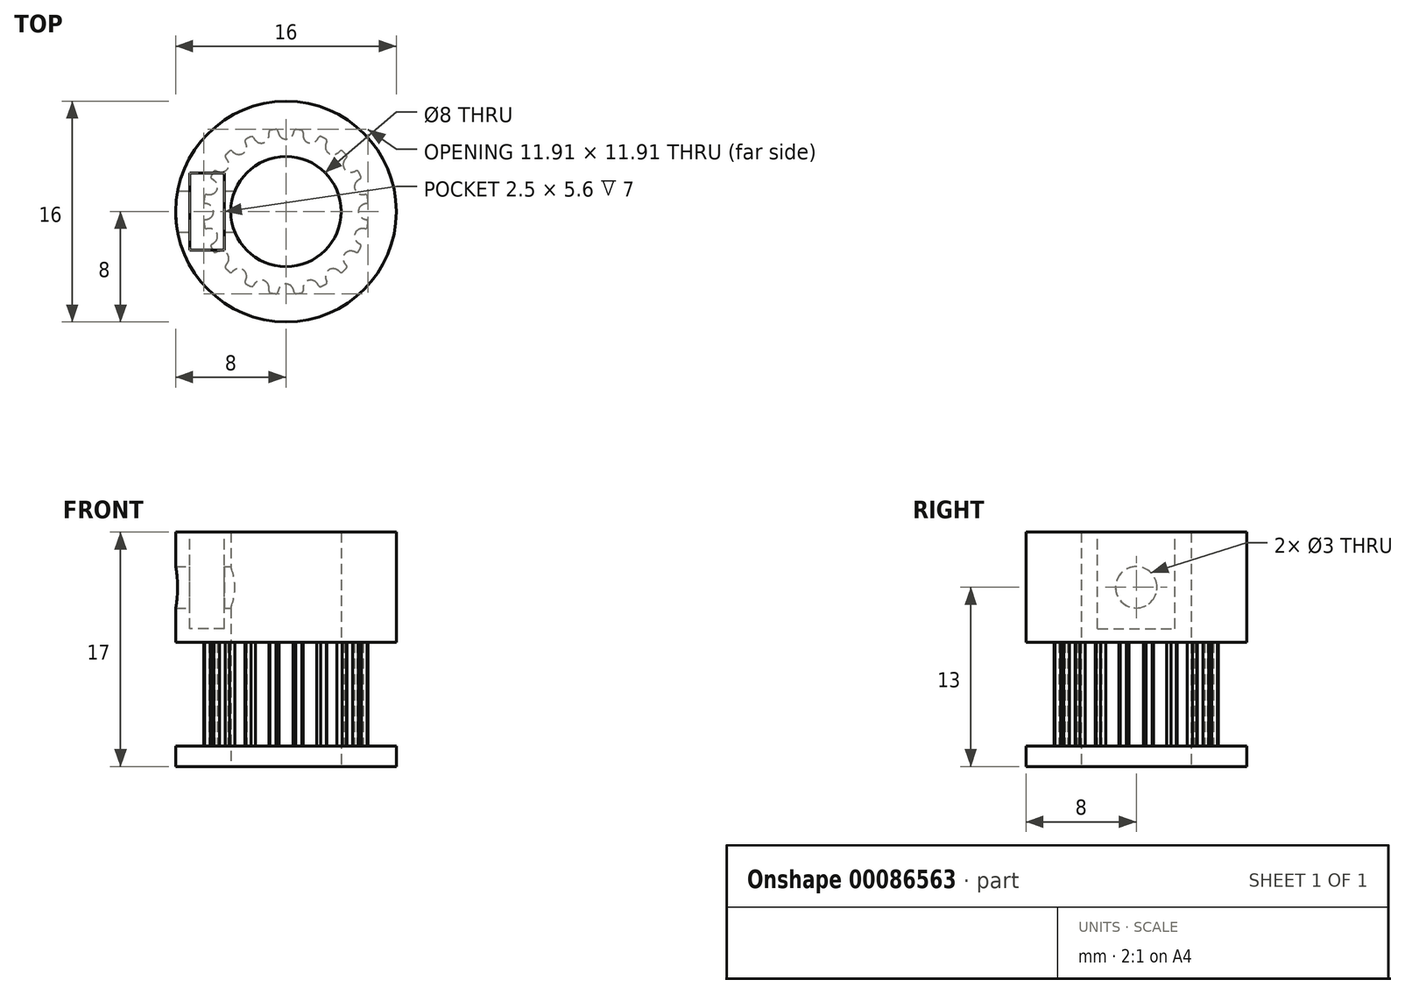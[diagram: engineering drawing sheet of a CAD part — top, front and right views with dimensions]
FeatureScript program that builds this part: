
annotation { "Feature Type Name" : "Feature", "Feature Type Description" : "" }
export const myFeature = defineFeature(function(context is Context, id is Id, definition is map)
    precondition{}
    {
        {
            var Q0;
            Q0=qCreatedBy(makeId("Top.planeOp"),FACE);
            var sketch = newSketch(context, id + "F0", { "sketchPlane" : qUnion([Q0])});
            skLineSegment(sketch, "E0", {"start": v(-19.17, 17.78) * mm, "end": v(-18.17, 17.78) * mm});
            skLineSegment(sketch, "E1", {"start": v(-18.17, 17.78) * mm, "end": v(-18.17, 18.4) * mm});
            skArc(sketch, "E2", {"start": v(-18.67, 18.85) * mm, "mid": v(-18.88, 19.07) * mm, "end": v(-19.17, 19.16) * mm});
            skArc(sketch, "E3", {"start": v(-18.58, 18.54) * mm, "mid": v(-18.61, 18.7) * mm, "end": v(-18.67, 18.85) * mm});
            skArc(sketch, "E4", {"start": v(-18.58, 18.54) * mm, "mid": v(-18.53, 18.44) * mm, "end": v(-18.43, 18.4) * mm});
            skLineSegment(sketch, "E5", {"start": v(-18.43, 18.4) * mm, "end": v(-18.17, 18.4) * mm});
            skArc(sketch, "E6.0.MirrorCS", {"start": v(-19.67, 18.85) * mm, "mid": v(-19.47, 19.07) * mm, "end": v(-19.17, 19.16) * mm});
            skArc(sketch, "E7.0.MirrorCS", {"start": v(-19.76, 18.54) * mm, "mid": v(-19.73, 18.7) * mm, "end": v(-19.67, 18.85) * mm});
            skArc(sketch, "E8.0.MirrorCS", {"start": v(-19.76, 18.54) * mm, "mid": v(-19.81, 18.44) * mm, "end": v(-19.91, 18.4) * mm});
            skLineSegment(sketch, "E9.0.MirrorCS", {"start": v(-19.91, 18.4) * mm, "end": v(-20.17, 18.4) * mm});
            skLineSegment(sketch, "E10.0.MirrorCS", {"start": v(-20.17, 17.78) * mm, "end": v(-20.17, 18.4) * mm});
            skLineSegment(sketch, "E11.0.MirrorCS", {"start": v(-19.17, 17.78) * mm, "end": v(-20.17, 17.78) * mm});
            skLineSegment(sketch, "E12.direction1", {"start": v(-20.17, 17.78) * mm, "end": v(-18.17, 17.78) * mm, "construction": true});
            skLineSegment(sketch, "E13", {"start": v(-20.17, 18.15) * mm, "end": v(-18.17, 18.15) * mm, "construction": true});
            skPoint(sketch, "E14", {"position": v(0, -5.25) * mm});
            skArc(sketch, "E15", {"start": v(0.51, -5.6) * mm, "mid": v(0, -5.25) * mm, "end": v(-0.51, -5.6) * mm});
            skArc(sketch, "E16", {"start": v(-0.51, -5.6) * mm, "mid": v(-0.56, -5.71) * mm, "end": v(-0.59, -5.83) * mm});
            skArc(sketch, "E17", {"start": v(0.59, -5.83) * mm, "mid": v(0.56, -5.71) * mm, "end": v(0.51, -5.6) * mm});
            skArc(sketch, "E18", {"start": v(0.72, -5.96) * mm, "mid": v(0.94, -5.93) * mm, "end": v(1.16, -5.89) * mm});
            skArc(sketch, "E19", {"start": v(0.59, -5.83) * mm, "mid": v(0.66, -5.94) * mm, "end": v(0.8, -5.95) * mm});
            skArc(sketch, "E20", {"start": v(-0.59, -5.83) * mm, "mid": v(-0.66, -5.94) * mm, "end": v(-0.8, -5.95) * mm});
            skArc(sketch, "E21.1.0", {"start": v(2.22, -5.16) * mm, "mid": v(1.62, -5) * mm, "end": v(1.24, -5.48) * mm});
            skPoint(sketch, "E21.1.1", {"position": v(1.62, -5) * mm});
            skArc(sketch, "E21.1.2", {"start": v(1.24, -5.48) * mm, "mid": v(1.23, -5.6) * mm, "end": v(1.24, -5.73) * mm});
            skArc(sketch, "E21.1.3", {"start": v(2.36, -5.37) * mm, "mid": v(2.47, -5.44) * mm, "end": v(2.6, -5.41) * mm});
            skArc(sketch, "E21.1.4", {"start": v(1.24, -5.73) * mm, "mid": v(1.2, -5.85) * mm, "end": v(1.08, -5.9) * mm});
            skArc(sketch, "E21.1.5", {"start": v(2.36, -5.37) * mm, "mid": v(2.3, -5.26) * mm, "end": v(2.22, -5.16) * mm});
            skArc(sketch, "E22.3.2.0", {"start": v(3.7, -4.22) * mm, "mid": v(3.09, -4.25) * mm, "end": v(2.87, -4.83) * mm});
            skPoint(sketch, "E22.4.2.0", {"position": v(3.09, -4.25) * mm});
            skArc(sketch, "E22.5.2.0", {"start": v(2.87, -4.83) * mm, "mid": v(2.9, -4.95) * mm, "end": v(2.95, -5.07) * mm});
            skArc(sketch, "E22.9.2.0", {"start": v(3.9, -4.37) * mm, "mid": v(4.03, -4.41) * mm, "end": v(4.14, -4.35) * mm});
            skArc(sketch, "E22.13.2.0", {"start": v(2.95, -5.07) * mm, "mid": v(2.95, -5.2) * mm, "end": v(2.85, -5.28) * mm});
            skArc(sketch, "E22.17.2.0", {"start": v(3.9, -4.37) * mm, "mid": v(3.81, -4.3) * mm, "end": v(3.7, -4.22) * mm});
            skArc(sketch, "E22.3.3.0", {"start": v(4.83, -2.87) * mm, "mid": v(4.25, -3.09) * mm, "end": v(4.22, -3.7) * mm});
            skPoint(sketch, "E22.4.3.0", {"position": v(4.25, -3.09) * mm});
            skArc(sketch, "E22.5.3.0", {"start": v(4.22, -3.7) * mm, "mid": v(4.3, -3.81) * mm, "end": v(4.37, -3.9) * mm});
            skArc(sketch, "E22.9.3.0", {"start": v(5.07, -2.95) * mm, "mid": v(5.2, -2.95) * mm, "end": v(5.28, -2.85) * mm});
            skArc(sketch, "E22.13.3.0", {"start": v(4.37, -3.9) * mm, "mid": v(4.41, -4.03) * mm, "end": v(4.35, -4.14) * mm});
            skArc(sketch, "E22.17.3.0", {"start": v(5.07, -2.95) * mm, "mid": v(4.95, -2.9) * mm, "end": v(4.83, -2.87) * mm});
            skArc(sketch, "E22.3.4.0", {"start": v(5.48, -1.24) * mm, "mid": v(5, -1.62) * mm, "end": v(5.16, -2.22) * mm});
            skPoint(sketch, "E22.4.4.0", {"position": v(5, -1.62) * mm});
            skArc(sketch, "E22.5.4.0", {"start": v(5.16, -2.22) * mm, "mid": v(5.26, -2.3) * mm, "end": v(5.37, -2.36) * mm});
            skArc(sketch, "E22.9.4.0", {"start": v(5.73, -1.24) * mm, "mid": v(5.85, -1.2) * mm, "end": v(5.9, -1.08) * mm});
            skArc(sketch, "E22.13.4.0", {"start": v(5.37, -2.36) * mm, "mid": v(5.44, -2.47) * mm, "end": v(5.41, -2.6) * mm});
            skArc(sketch, "E22.17.4.0", {"start": v(5.73, -1.24) * mm, "mid": v(5.6, -1.23) * mm, "end": v(5.48, -1.24) * mm});
            skArc(sketch, "E22.3.5.0", {"start": v(5.6, 0.51) * mm, "mid": v(5.25, 0) * mm, "end": v(5.6, -0.51) * mm});
            skPoint(sketch, "E22.4.5.0", {"position": v(5.25, 0) * mm});
            skArc(sketch, "E22.5.5.0", {"start": v(5.6, -0.51) * mm, "mid": v(5.71, -0.56) * mm, "end": v(5.83, -0.59) * mm});
            skArc(sketch, "E22.9.5.0", {"start": v(5.83, 0.59) * mm, "mid": v(5.94, 0.66) * mm, "end": v(5.95, 0.8) * mm});
            skArc(sketch, "E22.13.5.0", {"start": v(5.83, -0.59) * mm, "mid": v(5.94, -0.66) * mm, "end": v(5.95, -0.8) * mm});
            skArc(sketch, "E22.17.5.0", {"start": v(5.83, 0.59) * mm, "mid": v(5.71, 0.56) * mm, "end": v(5.6, 0.51) * mm});
            skArc(sketch, "E22.3.6.0", {"start": v(5.16, 2.22) * mm, "mid": v(5, 1.62) * mm, "end": v(5.48, 1.24) * mm});
            skPoint(sketch, "E22.4.6.0", {"position": v(5, 1.62) * mm});
            skArc(sketch, "E22.5.6.0", {"start": v(5.48, 1.24) * mm, "mid": v(5.6, 1.23) * mm, "end": v(5.73, 1.24) * mm});
            skArc(sketch, "E22.9.6.0", {"start": v(5.37, 2.36) * mm, "mid": v(5.44, 2.47) * mm, "end": v(5.41, 2.6) * mm});
            skArc(sketch, "E22.13.6.0", {"start": v(5.73, 1.24) * mm, "mid": v(5.85, 1.2) * mm, "end": v(5.9, 1.08) * mm});
            skArc(sketch, "E22.17.6.0", {"start": v(5.37, 2.36) * mm, "mid": v(5.26, 2.3) * mm, "end": v(5.16, 2.22) * mm});
            skArc(sketch, "E22.3.7.0", {"start": v(4.22, 3.7) * mm, "mid": v(4.25, 3.09) * mm, "end": v(4.83, 2.87) * mm});
            skPoint(sketch, "E22.4.7.0", {"position": v(4.25, 3.09) * mm});
            skArc(sketch, "E22.5.7.0", {"start": v(4.83, 2.87) * mm, "mid": v(4.95, 2.9) * mm, "end": v(5.07, 2.95) * mm});
            skArc(sketch, "E22.9.7.0", {"start": v(4.37, 3.9) * mm, "mid": v(4.41, 4.03) * mm, "end": v(4.35, 4.14) * mm});
            skArc(sketch, "E22.13.7.0", {"start": v(5.07, 2.95) * mm, "mid": v(5.2, 2.95) * mm, "end": v(5.28, 2.85) * mm});
            skArc(sketch, "E22.17.7.0", {"start": v(4.37, 3.9) * mm, "mid": v(4.3, 3.81) * mm, "end": v(4.22, 3.7) * mm});
            skArc(sketch, "E22.3.8.0", {"start": v(2.87, 4.83) * mm, "mid": v(3.09, 4.25) * mm, "end": v(3.7, 4.22) * mm});
            skPoint(sketch, "E22.4.8.0", {"position": v(3.09, 4.25) * mm});
            skArc(sketch, "E22.5.8.0", {"start": v(3.7, 4.22) * mm, "mid": v(3.81, 4.3) * mm, "end": v(3.9, 4.37) * mm});
            skArc(sketch, "E22.9.8.0", {"start": v(2.95, 5.07) * mm, "mid": v(2.95, 5.2) * mm, "end": v(2.85, 5.28) * mm});
            skArc(sketch, "E22.13.8.0", {"start": v(3.9, 4.37) * mm, "mid": v(4.03, 4.41) * mm, "end": v(4.14, 4.35) * mm});
            skArc(sketch, "E22.17.8.0", {"start": v(2.95, 5.07) * mm, "mid": v(2.9, 4.95) * mm, "end": v(2.87, 4.83) * mm});
            skArc(sketch, "E22.3.9.0", {"start": v(1.24, 5.48) * mm, "mid": v(1.62, 5) * mm, "end": v(2.22, 5.16) * mm});
            skPoint(sketch, "E22.4.9.0", {"position": v(1.62, 5) * mm});
            skArc(sketch, "E22.5.9.0", {"start": v(2.22, 5.16) * mm, "mid": v(2.3, 5.26) * mm, "end": v(2.36, 5.37) * mm});
            skArc(sketch, "E22.9.9.0", {"start": v(1.24, 5.73) * mm, "mid": v(1.2, 5.85) * mm, "end": v(1.08, 5.9) * mm});
            skArc(sketch, "E22.13.9.0", {"start": v(2.36, 5.37) * mm, "mid": v(2.47, 5.44) * mm, "end": v(2.6, 5.41) * mm});
            skArc(sketch, "E22.17.9.0", {"start": v(1.24, 5.73) * mm, "mid": v(1.23, 5.6) * mm, "end": v(1.24, 5.48) * mm});
            skArc(sketch, "E22.3.10.0", {"start": v(-0.51, 5.6) * mm, "mid": v(0, 5.25) * mm, "end": v(0.51, 5.6) * mm});
            skPoint(sketch, "E22.4.10.0", {"position": v(0, 5.25) * mm});
            skArc(sketch, "E22.5.10.0", {"start": v(0.51, 5.6) * mm, "mid": v(0.56, 5.71) * mm, "end": v(0.59, 5.83) * mm});
            skArc(sketch, "E22.9.10.0", {"start": v(-0.59, 5.83) * mm, "mid": v(-0.66, 5.94) * mm, "end": v(-0.8, 5.95) * mm});
            skArc(sketch, "E22.13.10.0", {"start": v(0.59, 5.83) * mm, "mid": v(0.66, 5.94) * mm, "end": v(0.8, 5.95) * mm});
            skArc(sketch, "E22.17.10.0", {"start": v(-0.59, 5.83) * mm, "mid": v(-0.56, 5.71) * mm, "end": v(-0.51, 5.6) * mm});
            skArc(sketch, "E22.3.11.0", {"start": v(-2.22, 5.16) * mm, "mid": v(-1.62, 5) * mm, "end": v(-1.24, 5.48) * mm});
            skPoint(sketch, "E22.4.11.0", {"position": v(-1.62, 5) * mm});
            skArc(sketch, "E22.5.11.0", {"start": v(-1.24, 5.48) * mm, "mid": v(-1.23, 5.6) * mm, "end": v(-1.24, 5.73) * mm});
            skArc(sketch, "E22.9.11.0", {"start": v(-2.36, 5.37) * mm, "mid": v(-2.47, 5.44) * mm, "end": v(-2.6, 5.41) * mm});
            skArc(sketch, "E22.13.11.0", {"start": v(-1.24, 5.73) * mm, "mid": v(-1.2, 5.85) * mm, "end": v(-1.08, 5.9) * mm});
            skArc(sketch, "E22.17.11.0", {"start": v(-2.36, 5.37) * mm, "mid": v(-2.3, 5.26) * mm, "end": v(-2.22, 5.16) * mm});
            skArc(sketch, "E22.3.12.0", {"start": v(-3.7, 4.22) * mm, "mid": v(-3.09, 4.25) * mm, "end": v(-2.87, 4.83) * mm});
            skPoint(sketch, "E22.4.12.0", {"position": v(-3.09, 4.25) * mm});
            skArc(sketch, "E22.5.12.0", {"start": v(-2.87, 4.83) * mm, "mid": v(-2.9, 4.95) * mm, "end": v(-2.95, 5.07) * mm});
            skArc(sketch, "E22.9.12.0", {"start": v(-3.9, 4.37) * mm, "mid": v(-4.03, 4.41) * mm, "end": v(-4.14, 4.35) * mm});
            skArc(sketch, "E22.13.12.0", {"start": v(-2.95, 5.07) * mm, "mid": v(-2.95, 5.2) * mm, "end": v(-2.85, 5.28) * mm});
            skArc(sketch, "E22.17.12.0", {"start": v(-3.9, 4.37) * mm, "mid": v(-3.81, 4.3) * mm, "end": v(-3.7, 4.22) * mm});
            skArc(sketch, "E22.3.13.0", {"start": v(-4.83, 2.87) * mm, "mid": v(-4.25, 3.09) * mm, "end": v(-4.22, 3.7) * mm});
            skPoint(sketch, "E22.4.13.0", {"position": v(-4.25, 3.09) * mm});
            skArc(sketch, "E22.5.13.0", {"start": v(-4.22, 3.7) * mm, "mid": v(-4.3, 3.81) * mm, "end": v(-4.37, 3.9) * mm});
            skArc(sketch, "E22.9.13.0", {"start": v(-5.07, 2.95) * mm, "mid": v(-5.2, 2.95) * mm, "end": v(-5.28, 2.85) * mm});
            skArc(sketch, "E22.13.13.0", {"start": v(-4.37, 3.9) * mm, "mid": v(-4.41, 4.03) * mm, "end": v(-4.35, 4.14) * mm});
            skArc(sketch, "E22.17.13.0", {"start": v(-5.07, 2.95) * mm, "mid": v(-4.95, 2.9) * mm, "end": v(-4.83, 2.87) * mm});
            skArc(sketch, "E22.3.14.0", {"start": v(-5.48, 1.24) * mm, "mid": v(-5, 1.62) * mm, "end": v(-5.16, 2.22) * mm});
            skPoint(sketch, "E22.4.14.0", {"position": v(-5, 1.62) * mm});
            skArc(sketch, "E22.5.14.0", {"start": v(-5.16, 2.22) * mm, "mid": v(-5.26, 2.3) * mm, "end": v(-5.37, 2.36) * mm});
            skArc(sketch, "E22.9.14.0", {"start": v(-5.73, 1.24) * mm, "mid": v(-5.85, 1.2) * mm, "end": v(-5.9, 1.08) * mm});
            skArc(sketch, "E22.13.14.0", {"start": v(-5.37, 2.36) * mm, "mid": v(-5.44, 2.47) * mm, "end": v(-5.41, 2.6) * mm});
            skArc(sketch, "E22.17.14.0", {"start": v(-5.73, 1.24) * mm, "mid": v(-5.6, 1.23) * mm, "end": v(-5.48, 1.24) * mm});
            skArc(sketch, "E22.3.15.0", {"start": v(-5.6, -0.51) * mm, "mid": v(-5.25, 0) * mm, "end": v(-5.6, 0.51) * mm});
            skPoint(sketch, "E22.4.15.0", {"position": v(-5.25, 0) * mm});
            skArc(sketch, "E22.5.15.0", {"start": v(-5.6, 0.51) * mm, "mid": v(-5.71, 0.56) * mm, "end": v(-5.83, 0.59) * mm});
            skArc(sketch, "E22.9.15.0", {"start": v(-5.83, -0.59) * mm, "mid": v(-5.94, -0.66) * mm, "end": v(-5.95, -0.8) * mm});
            skArc(sketch, "E22.13.15.0", {"start": v(-5.83, 0.59) * mm, "mid": v(-5.94, 0.66) * mm, "end": v(-5.95, 0.8) * mm});
            skArc(sketch, "E22.17.15.0", {"start": v(-5.83, -0.59) * mm, "mid": v(-5.71, -0.56) * mm, "end": v(-5.6, -0.51) * mm});
            skArc(sketch, "E22.3.16.0", {"start": v(-5.16, -2.22) * mm, "mid": v(-5, -1.62) * mm, "end": v(-5.48, -1.24) * mm});
            skPoint(sketch, "E22.4.16.0", {"position": v(-5, -1.62) * mm});
            skArc(sketch, "E22.5.16.0", {"start": v(-5.48, -1.24) * mm, "mid": v(-5.6, -1.23) * mm, "end": v(-5.73, -1.24) * mm});
            skArc(sketch, "E22.9.16.0", {"start": v(-5.37, -2.36) * mm, "mid": v(-5.44, -2.47) * mm, "end": v(-5.41, -2.6) * mm});
            skArc(sketch, "E22.13.16.0", {"start": v(-5.73, -1.24) * mm, "mid": v(-5.85, -1.2) * mm, "end": v(-5.9, -1.08) * mm});
            skArc(sketch, "E22.17.16.0", {"start": v(-5.37, -2.36) * mm, "mid": v(-5.26, -2.3) * mm, "end": v(-5.16, -2.22) * mm});
            skArc(sketch, "E22.3.17.0", {"start": v(-4.22, -3.7) * mm, "mid": v(-4.25, -3.09) * mm, "end": v(-4.83, -2.87) * mm});
            skPoint(sketch, "E22.4.17.0", {"position": v(-4.25, -3.09) * mm});
            skArc(sketch, "E22.5.17.0", {"start": v(-4.83, -2.87) * mm, "mid": v(-4.95, -2.9) * mm, "end": v(-5.07, -2.95) * mm});
            skArc(sketch, "E22.9.17.0", {"start": v(-4.37, -3.9) * mm, "mid": v(-4.41, -4.03) * mm, "end": v(-4.35, -4.14) * mm});
            skArc(sketch, "E22.13.17.0", {"start": v(-5.07, -2.95) * mm, "mid": v(-5.2, -2.95) * mm, "end": v(-5.28, -2.85) * mm});
            skArc(sketch, "E22.17.17.0", {"start": v(-4.37, -3.9) * mm, "mid": v(-4.3, -3.81) * mm, "end": v(-4.22, -3.7) * mm});
            skArc(sketch, "E22.3.18.0", {"start": v(-2.87, -4.83) * mm, "mid": v(-3.09, -4.25) * mm, "end": v(-3.7, -4.22) * mm});
            skPoint(sketch, "E22.4.18.0", {"position": v(-3.09, -4.25) * mm});
            skArc(sketch, "E22.5.18.0", {"start": v(-3.7, -4.22) * mm, "mid": v(-3.81, -4.3) * mm, "end": v(-3.9, -4.37) * mm});
            skArc(sketch, "E22.9.18.0", {"start": v(-2.95, -5.07) * mm, "mid": v(-2.95, -5.2) * mm, "end": v(-2.85, -5.28) * mm});
            skArc(sketch, "E22.13.18.0", {"start": v(-3.9, -4.37) * mm, "mid": v(-4.03, -4.41) * mm, "end": v(-4.14, -4.35) * mm});
            skArc(sketch, "E22.17.18.0", {"start": v(-2.95, -5.07) * mm, "mid": v(-2.9, -4.95) * mm, "end": v(-2.87, -4.83) * mm});
            skArc(sketch, "E22.3.19.0", {"start": v(-1.24, -5.48) * mm, "mid": v(-1.62, -5) * mm, "end": v(-2.22, -5.16) * mm});
            skPoint(sketch, "E22.4.19.0", {"position": v(-1.62, -5) * mm});
            skArc(sketch, "E22.5.19.0", {"start": v(-2.22, -5.16) * mm, "mid": v(-2.3, -5.26) * mm, "end": v(-2.36, -5.37) * mm});
            skArc(sketch, "E22.9.19.0", {"start": v(-1.24, -5.73) * mm, "mid": v(-1.2, -5.85) * mm, "end": v(-1.08, -5.9) * mm});
            skArc(sketch, "E22.13.19.0", {"start": v(-2.36, -5.37) * mm, "mid": v(-2.47, -5.44) * mm, "end": v(-2.6, -5.41) * mm});
            skArc(sketch, "E22.17.19.0", {"start": v(-1.24, -5.73) * mm, "mid": v(-1.23, -5.6) * mm, "end": v(-1.24, -5.48) * mm});
            skArc(sketch, "E23.trimOffspring", {"start": v(2.52, -5.44) * mm, "mid": v(2.72, -5.35) * mm, "end": v(2.92, -5.24) * mm});
            skArc(sketch, "E24.trimOffspring", {"start": v(4.08, -4.4) * mm, "mid": v(4.24, -4.24) * mm, "end": v(4.4, -4.08) * mm});
            skArc(sketch, "E25.trimOffspring", {"start": v(5.24, -2.92) * mm, "mid": v(5.33, -2.76) * mm, "end": v(5.41, -2.6) * mm});
            skArc(sketch, "E26.trimOffspring", {"start": v(5.89, -1.16) * mm, "mid": v(5.93, -0.94) * mm, "end": v(5.96, -0.72) * mm});
            skArc(sketch, "E27.trimOffspring", {"start": v(5.44, 2.52) * mm, "mid": v(5.35, 2.72) * mm, "end": v(5.24, 2.92) * mm});
            skArc(sketch, "E28.trimOffspring", {"start": v(4.4, 4.08) * mm, "mid": v(4.24, 4.24) * mm, "end": v(4.08, 4.4) * mm});
            skArc(sketch, "E29.trimOffspring", {"start": v(5.96, 0.72) * mm, "mid": v(5.93, 0.94) * mm, "end": v(5.89, 1.16) * mm});
            skArc(sketch, "E30.trimOffspring", {"start": v(2.92, 5.24) * mm, "mid": v(2.72, 5.35) * mm, "end": v(2.52, 5.44) * mm});
            skArc(sketch, "E31.trimOffspring", {"start": v(1.16, 5.89) * mm, "mid": v(0.94, 5.93) * mm, "end": v(0.72, 5.96) * mm});
            skArc(sketch, "E32.trimOffspring", {"start": v(-0.72, 5.96) * mm, "mid": v(-0.94, 5.93) * mm, "end": v(-1.16, 5.89) * mm});
            skArc(sketch, "E33.trimOffspring", {"start": v(-2.52, 5.44) * mm, "mid": v(-2.72, 5.35) * mm, "end": v(-2.92, 5.24) * mm});
            skArc(sketch, "E34.trimOffspring", {"start": v(-4.08, 4.4) * mm, "mid": v(-4.24, 4.24) * mm, "end": v(-4.4, 4.08) * mm});
            skArc(sketch, "E35.trimOffspring", {"start": v(-5.24, 2.92) * mm, "mid": v(-5.35, 2.72) * mm, "end": v(-5.44, 2.52) * mm});
            skArc(sketch, "E36.trimOffspring", {"start": v(-5.89, 1.16) * mm, "mid": v(-5.93, 0.94) * mm, "end": v(-5.96, 0.72) * mm});
            skArc(sketch, "E37.trimOffspring", {"start": v(-5.96, -0.72) * mm, "mid": v(-5.93, -0.94) * mm, "end": v(-5.89, -1.16) * mm});
            skArc(sketch, "E38.trimOffspring", {"start": v(-5.44, -2.52) * mm, "mid": v(-5.35, -2.72) * mm, "end": v(-5.24, -2.92) * mm});
            skArc(sketch, "E39.trimOffspring", {"start": v(-4.4, -4.08) * mm, "mid": v(-4.24, -4.24) * mm, "end": v(-4.08, -4.4) * mm});
            skArc(sketch, "E40.trimOffspring", {"start": v(-2.92, -5.24) * mm, "mid": v(-2.72, -5.35) * mm, "end": v(-2.52, -5.44) * mm});
            skArc(sketch, "E41.trimOffspring", {"start": v(-1.16, -5.89) * mm, "mid": v(-0.94, -5.93) * mm, "end": v(-0.72, -5.96) * mm});
            skSolve(sketch);
        }
        {
            var Q0;
            Q0=makeQuery(id+"F0.imprint","IMPRINT",FACE,{"disambiguationData":[TD([[makeQuery(id+"F0.imprint","IMPRINT",EDGE,{"derivedFrom":sQuery(id+"F0.wireOp",EDGE,"E15")}),-1.0]])]});
            extrude(context, id + "F1", {"entities" : qUnion([Q0]), "depth" : 7.5 * mm});
        }
        {
            var Q0;
            Q0=makeQuery(id+"F1.opExtrude","CAP_FACE",FACE,{"disambiguationData":[OSD([sQuery(id+"F0.wireOp",EDGE,"E15"),sQuery(id+"F0.wireOp",EDGE,"E16"),sQuery(id+"F0.wireOp",EDGE,"E17"),sQuery(id+"F0.wireOp",EDGE,"E18"),sQuery(id+"F0.wireOp",EDGE,"E19"),sQuery(id+"F0.wireOp",EDGE,"E20"),sQuery(id+"F0.wireOp",EDGE,"E21.1.0"),sQuery(id+"F0.wireOp",EDGE,"E21.1.2"),sQuery(id+"F0.wireOp",EDGE,"E21.1.3"),sQuery(id+"F0.wireOp",EDGE,"E21.1.4"),sQuery(id+"F0.wireOp",EDGE,"E21.1.5"),sQuery(id+"F0.wireOp",EDGE,"E22.3.2.0"),sQuery(id+"F0.wireOp",EDGE,"E22.5.2.0"),sQuery(id+"F0.wireOp",EDGE,"E22.9.2.0"),sQuery(id+"F0.wireOp",EDGE,"E22.13.2.0"),sQuery(id+"F0.wireOp",EDGE,"E22.17.2.0"),sQuery(id+"F0.wireOp",EDGE,"E22.3.3.0"),sQuery(id+"F0.wireOp",EDGE,"E22.5.3.0"),sQuery(id+"F0.wireOp",EDGE,"E22.9.3.0"),sQuery(id+"F0.wireOp",EDGE,"E22.13.3.0"),sQuery(id+"F0.wireOp",EDGE,"E22.17.3.0"),sQuery(id+"F0.wireOp",EDGE,"E22.3.4.0"),sQuery(id+"F0.wireOp",EDGE,"E22.5.4.0"),sQuery(id+"F0.wireOp",EDGE,"E22.9.4.0"),sQuery(id+"F0.wireOp",EDGE,"E22.13.4.0"),sQuery(id+"F0.wireOp",EDGE,"E22.17.4.0"),sQuery(id+"F0.wireOp",EDGE,"E22.3.5.0"),sQuery(id+"F0.wireOp",EDGE,"E22.5.5.0"),sQuery(id+"F0.wireOp",EDGE,"E22.9.5.0"),sQuery(id+"F0.wireOp",EDGE,"E22.13.5.0"),sQuery(id+"F0.wireOp",EDGE,"E22.17.5.0"),sQuery(id+"F0.wireOp",EDGE,"E22.3.6.0"),sQuery(id+"F0.wireOp",EDGE,"E22.5.6.0"),sQuery(id+"F0.wireOp",EDGE,"E22.9.6.0"),sQuery(id+"F0.wireOp",EDGE,"E22.13.6.0"),sQuery(id+"F0.wireOp",EDGE,"E22.17.6.0"),sQuery(id+"F0.wireOp",EDGE,"E22.3.7.0"),sQuery(id+"F0.wireOp",EDGE,"E22.5.7.0"),sQuery(id+"F0.wireOp",EDGE,"E22.9.7.0"),sQuery(id+"F0.wireOp",EDGE,"E22.13.7.0"),sQuery(id+"F0.wireOp",EDGE,"E22.17.7.0"),sQuery(id+"F0.wireOp",EDGE,"E22.3.8.0"),sQuery(id+"F0.wireOp",EDGE,"E22.5.8.0"),sQuery(id+"F0.wireOp",EDGE,"E22.9.8.0"),sQuery(id+"F0.wireOp",EDGE,"E22.13.8.0"),sQuery(id+"F0.wireOp",EDGE,"E22.17.8.0"),sQuery(id+"F0.wireOp",EDGE,"E22.3.9.0"),sQuery(id+"F0.wireOp",EDGE,"E22.5.9.0"),sQuery(id+"F0.wireOp",EDGE,"E22.9.9.0"),sQuery(id+"F0.wireOp",EDGE,"E22.13.9.0"),sQuery(id+"F0.wireOp",EDGE,"E22.17.9.0"),sQuery(id+"F0.wireOp",EDGE,"E22.3.10.0"),sQuery(id+"F0.wireOp",EDGE,"E22.5.10.0"),sQuery(id+"F0.wireOp",EDGE,"E22.9.10.0"),sQuery(id+"F0.wireOp",EDGE,"E22.13.10.0"),sQuery(id+"F0.wireOp",EDGE,"E22.17.10.0"),sQuery(id+"F0.wireOp",EDGE,"E22.3.11.0"),sQuery(id+"F0.wireOp",EDGE,"E22.5.11.0"),sQuery(id+"F0.wireOp",EDGE,"E22.9.11.0"),sQuery(id+"F0.wireOp",EDGE,"E22.13.11.0"),sQuery(id+"F0.wireOp",EDGE,"E22.17.11.0"),sQuery(id+"F0.wireOp",EDGE,"E22.3.12.0"),sQuery(id+"F0.wireOp",EDGE,"E22.5.12.0"),sQuery(id+"F0.wireOp",EDGE,"E22.9.12.0"),sQuery(id+"F0.wireOp",EDGE,"E22.13.12.0"),sQuery(id+"F0.wireOp",EDGE,"E22.17.12.0"),sQuery(id+"F0.wireOp",EDGE,"E22.3.13.0"),sQuery(id+"F0.wireOp",EDGE,"E22.5.13.0"),sQuery(id+"F0.wireOp",EDGE,"E22.9.13.0"),sQuery(id+"F0.wireOp",EDGE,"E22.13.13.0"),sQuery(id+"F0.wireOp",EDGE,"E22.17.13.0"),sQuery(id+"F0.wireOp",EDGE,"E22.3.14.0"),sQuery(id+"F0.wireOp",EDGE,"E22.5.14.0"),sQuery(id+"F0.wireOp",EDGE,"E22.9.14.0"),sQuery(id+"F0.wireOp",EDGE,"E22.13.14.0"),sQuery(id+"F0.wireOp",EDGE,"E22.17.14.0"),sQuery(id+"F0.wireOp",EDGE,"E22.3.15.0"),sQuery(id+"F0.wireOp",EDGE,"E22.5.15.0"),sQuery(id+"F0.wireOp",EDGE,"E22.9.15.0"),sQuery(id+"F0.wireOp",EDGE,"E22.13.15.0"),sQuery(id+"F0.wireOp",EDGE,"E22.17.15.0"),sQuery(id+"F0.wireOp",EDGE,"E22.3.16.0"),sQuery(id+"F0.wireOp",EDGE,"E22.5.16.0"),sQuery(id+"F0.wireOp",EDGE,"E22.9.16.0"),sQuery(id+"F0.wireOp",EDGE,"E22.13.16.0"),sQuery(id+"F0.wireOp",EDGE,"E22.17.16.0"),sQuery(id+"F0.wireOp",EDGE,"E22.3.17.0"),sQuery(id+"F0.wireOp",EDGE,"E22.5.17.0"),sQuery(id+"F0.wireOp",EDGE,"E22.9.17.0"),sQuery(id+"F0.wireOp",EDGE,"E22.13.17.0"),sQuery(id+"F0.wireOp",EDGE,"E22.17.17.0"),sQuery(id+"F0.wireOp",EDGE,"E22.3.18.0"),sQuery(id+"F0.wireOp",EDGE,"E22.5.18.0"),sQuery(id+"F0.wireOp",EDGE,"E22.9.18.0"),sQuery(id+"F0.wireOp",EDGE,"E22.13.18.0"),sQuery(id+"F0.wireOp",EDGE,"E22.17.18.0"),sQuery(id+"F0.wireOp",EDGE,"E22.3.19.0"),sQuery(id+"F0.wireOp",EDGE,"E22.5.19.0"),sQuery(id+"F0.wireOp",EDGE,"E22.9.19.0"),sQuery(id+"F0.wireOp",EDGE,"E22.13.19.0"),sQuery(id+"F0.wireOp",EDGE,"E22.17.19.0"),sQuery(id+"F0.wireOp",EDGE,"E23.trimOffspring"),sQuery(id+"F0.wireOp",EDGE,"E24.trimOffspring"),sQuery(id+"F0.wireOp",EDGE,"E25.trimOffspring"),sQuery(id+"F0.wireOp",EDGE,"E26.trimOffspring"),sQuery(id+"F0.wireOp",EDGE,"E27.trimOffspring"),sQuery(id+"F0.wireOp",EDGE,"E28.trimOffspring"),sQuery(id+"F0.wireOp",EDGE,"E29.trimOffspring"),sQuery(id+"F0.wireOp",EDGE,"E30.trimOffspring"),sQuery(id+"F0.wireOp",EDGE,"E31.trimOffspring"),sQuery(id+"F0.wireOp",EDGE,"E32.trimOffspring"),sQuery(id+"F0.wireOp",EDGE,"E33.trimOffspring"),sQuery(id+"F0.wireOp",EDGE,"E34.trimOffspring"),sQuery(id+"F0.wireOp",EDGE,"E35.trimOffspring"),sQuery(id+"F0.wireOp",EDGE,"E36.trimOffspring"),sQuery(id+"F0.wireOp",EDGE,"E37.trimOffspring"),sQuery(id+"F0.wireOp",EDGE,"E38.trimOffspring"),sQuery(id+"F0.wireOp",EDGE,"E39.trimOffspring"),sQuery(id+"F0.wireOp",EDGE,"E40.trimOffspring"),sQuery(id+"F0.wireOp",EDGE,"E41.trimOffspring")])],"isStart":false});
            var sketch = newSketch(context, id + "F2", { "sketchPlane" : qUnion([Q0])});
            skCircle(sketch, "E42", {"center": v(0, 0) * mm, "radius": 8 * mm});
            skSolve(sketch);
        }
        {
            var Q0;
            Q0=qSketchRegion(id+"F2",true);
            extrude(context, id + "F3", {"entities" : qUnion([Q0]), "operationType" : NewBodyOperationType.ADD, "depth" : 8 * mm});
        }
        {
            var Q0;
            Q0=makeQuery(id+"F1.opExtrude","CAP_FACE",FACE,{"disambiguationData":[OSD([sQuery(id+"F0.wireOp",EDGE,"E15"),sQuery(id+"F0.wireOp",EDGE,"E16"),sQuery(id+"F0.wireOp",EDGE,"E17"),sQuery(id+"F0.wireOp",EDGE,"E18"),sQuery(id+"F0.wireOp",EDGE,"E19"),sQuery(id+"F0.wireOp",EDGE,"E20"),sQuery(id+"F0.wireOp",EDGE,"E21.1.0"),sQuery(id+"F0.wireOp",EDGE,"E21.1.2"),sQuery(id+"F0.wireOp",EDGE,"E21.1.3"),sQuery(id+"F0.wireOp",EDGE,"E21.1.4"),sQuery(id+"F0.wireOp",EDGE,"E21.1.5"),sQuery(id+"F0.wireOp",EDGE,"E22.3.2.0"),sQuery(id+"F0.wireOp",EDGE,"E22.5.2.0"),sQuery(id+"F0.wireOp",EDGE,"E22.9.2.0"),sQuery(id+"F0.wireOp",EDGE,"E22.13.2.0"),sQuery(id+"F0.wireOp",EDGE,"E22.17.2.0"),sQuery(id+"F0.wireOp",EDGE,"E22.3.3.0"),sQuery(id+"F0.wireOp",EDGE,"E22.5.3.0"),sQuery(id+"F0.wireOp",EDGE,"E22.9.3.0"),sQuery(id+"F0.wireOp",EDGE,"E22.13.3.0"),sQuery(id+"F0.wireOp",EDGE,"E22.17.3.0"),sQuery(id+"F0.wireOp",EDGE,"E22.3.4.0"),sQuery(id+"F0.wireOp",EDGE,"E22.5.4.0"),sQuery(id+"F0.wireOp",EDGE,"E22.9.4.0"),sQuery(id+"F0.wireOp",EDGE,"E22.13.4.0"),sQuery(id+"F0.wireOp",EDGE,"E22.17.4.0"),sQuery(id+"F0.wireOp",EDGE,"E22.3.5.0"),sQuery(id+"F0.wireOp",EDGE,"E22.5.5.0"),sQuery(id+"F0.wireOp",EDGE,"E22.9.5.0"),sQuery(id+"F0.wireOp",EDGE,"E22.13.5.0"),sQuery(id+"F0.wireOp",EDGE,"E22.17.5.0"),sQuery(id+"F0.wireOp",EDGE,"E22.3.6.0"),sQuery(id+"F0.wireOp",EDGE,"E22.5.6.0"),sQuery(id+"F0.wireOp",EDGE,"E22.9.6.0"),sQuery(id+"F0.wireOp",EDGE,"E22.13.6.0"),sQuery(id+"F0.wireOp",EDGE,"E22.17.6.0"),sQuery(id+"F0.wireOp",EDGE,"E22.3.7.0"),sQuery(id+"F0.wireOp",EDGE,"E22.5.7.0"),sQuery(id+"F0.wireOp",EDGE,"E22.9.7.0"),sQuery(id+"F0.wireOp",EDGE,"E22.13.7.0"),sQuery(id+"F0.wireOp",EDGE,"E22.17.7.0"),sQuery(id+"F0.wireOp",EDGE,"E22.3.8.0"),sQuery(id+"F0.wireOp",EDGE,"E22.5.8.0"),sQuery(id+"F0.wireOp",EDGE,"E22.9.8.0"),sQuery(id+"F0.wireOp",EDGE,"E22.13.8.0"),sQuery(id+"F0.wireOp",EDGE,"E22.17.8.0"),sQuery(id+"F0.wireOp",EDGE,"E22.3.9.0"),sQuery(id+"F0.wireOp",EDGE,"E22.5.9.0"),sQuery(id+"F0.wireOp",EDGE,"E22.9.9.0"),sQuery(id+"F0.wireOp",EDGE,"E22.13.9.0"),sQuery(id+"F0.wireOp",EDGE,"E22.17.9.0"),sQuery(id+"F0.wireOp",EDGE,"E22.3.10.0"),sQuery(id+"F0.wireOp",EDGE,"E22.5.10.0"),sQuery(id+"F0.wireOp",EDGE,"E22.9.10.0"),sQuery(id+"F0.wireOp",EDGE,"E22.13.10.0"),sQuery(id+"F0.wireOp",EDGE,"E22.17.10.0"),sQuery(id+"F0.wireOp",EDGE,"E22.3.11.0"),sQuery(id+"F0.wireOp",EDGE,"E22.5.11.0"),sQuery(id+"F0.wireOp",EDGE,"E22.9.11.0"),sQuery(id+"F0.wireOp",EDGE,"E22.13.11.0"),sQuery(id+"F0.wireOp",EDGE,"E22.17.11.0"),sQuery(id+"F0.wireOp",EDGE,"E22.3.12.0"),sQuery(id+"F0.wireOp",EDGE,"E22.5.12.0"),sQuery(id+"F0.wireOp",EDGE,"E22.9.12.0"),sQuery(id+"F0.wireOp",EDGE,"E22.13.12.0"),sQuery(id+"F0.wireOp",EDGE,"E22.17.12.0"),sQuery(id+"F0.wireOp",EDGE,"E22.3.13.0"),sQuery(id+"F0.wireOp",EDGE,"E22.5.13.0"),sQuery(id+"F0.wireOp",EDGE,"E22.9.13.0"),sQuery(id+"F0.wireOp",EDGE,"E22.13.13.0"),sQuery(id+"F0.wireOp",EDGE,"E22.17.13.0"),sQuery(id+"F0.wireOp",EDGE,"E22.3.14.0"),sQuery(id+"F0.wireOp",EDGE,"E22.5.14.0"),sQuery(id+"F0.wireOp",EDGE,"E22.9.14.0"),sQuery(id+"F0.wireOp",EDGE,"E22.13.14.0"),sQuery(id+"F0.wireOp",EDGE,"E22.17.14.0"),sQuery(id+"F0.wireOp",EDGE,"E22.3.15.0"),sQuery(id+"F0.wireOp",EDGE,"E22.5.15.0"),sQuery(id+"F0.wireOp",EDGE,"E22.9.15.0"),sQuery(id+"F0.wireOp",EDGE,"E22.13.15.0"),sQuery(id+"F0.wireOp",EDGE,"E22.17.15.0"),sQuery(id+"F0.wireOp",EDGE,"E22.3.16.0"),sQuery(id+"F0.wireOp",EDGE,"E22.5.16.0"),sQuery(id+"F0.wireOp",EDGE,"E22.9.16.0"),sQuery(id+"F0.wireOp",EDGE,"E22.13.16.0"),sQuery(id+"F0.wireOp",EDGE,"E22.17.16.0"),sQuery(id+"F0.wireOp",EDGE,"E22.3.17.0"),sQuery(id+"F0.wireOp",EDGE,"E22.5.17.0"),sQuery(id+"F0.wireOp",EDGE,"E22.9.17.0"),sQuery(id+"F0.wireOp",EDGE,"E22.13.17.0"),sQuery(id+"F0.wireOp",EDGE,"E22.17.17.0"),sQuery(id+"F0.wireOp",EDGE,"E22.3.18.0"),sQuery(id+"F0.wireOp",EDGE,"E22.5.18.0"),sQuery(id+"F0.wireOp",EDGE,"E22.9.18.0"),sQuery(id+"F0.wireOp",EDGE,"E22.13.18.0"),sQuery(id+"F0.wireOp",EDGE,"E22.17.18.0"),sQuery(id+"F0.wireOp",EDGE,"E22.3.19.0"),sQuery(id+"F0.wireOp",EDGE,"E22.5.19.0"),sQuery(id+"F0.wireOp",EDGE,"E22.9.19.0"),sQuery(id+"F0.wireOp",EDGE,"E22.13.19.0"),sQuery(id+"F0.wireOp",EDGE,"E22.17.19.0"),sQuery(id+"F0.wireOp",EDGE,"E23.trimOffspring"),sQuery(id+"F0.wireOp",EDGE,"E24.trimOffspring"),sQuery(id+"F0.wireOp",EDGE,"E25.trimOffspring"),sQuery(id+"F0.wireOp",EDGE,"E26.trimOffspring"),sQuery(id+"F0.wireOp",EDGE,"E27.trimOffspring"),sQuery(id+"F0.wireOp",EDGE,"E28.trimOffspring"),sQuery(id+"F0.wireOp",EDGE,"E29.trimOffspring"),sQuery(id+"F0.wireOp",EDGE,"E30.trimOffspring"),sQuery(id+"F0.wireOp",EDGE,"E31.trimOffspring"),sQuery(id+"F0.wireOp",EDGE,"E32.trimOffspring"),sQuery(id+"F0.wireOp",EDGE,"E33.trimOffspring"),sQuery(id+"F0.wireOp",EDGE,"E34.trimOffspring"),sQuery(id+"F0.wireOp",EDGE,"E35.trimOffspring"),sQuery(id+"F0.wireOp",EDGE,"E36.trimOffspring"),sQuery(id+"F0.wireOp",EDGE,"E37.trimOffspring"),sQuery(id+"F0.wireOp",EDGE,"E38.trimOffspring"),sQuery(id+"F0.wireOp",EDGE,"E39.trimOffspring"),sQuery(id+"F0.wireOp",EDGE,"E40.trimOffspring"),sQuery(id+"F0.wireOp",EDGE,"E41.trimOffspring")])],"isStart":true});
            var sketch = newSketch(context, id + "F4", { "sketchPlane" : qUnion([Q0])});
            skCircle(sketch, "E43", {"center": v(0, 0) * mm, "radius": 8 * mm});
            skSolve(sketch);
        }
        {
            var Q0;
            Q0=qSketchRegion(id+"F4",true);
            extrude(context, id + "F5", {"entities" : qUnion([Q0]), "operationType" : NewBodyOperationType.ADD, "depth" : 1.5 * mm});
        }
        {
            var Q0;
            Q0=makeQuery(id+"F5.opExtrude","CAP_FACE",FACE,{"disambiguationData":[OSD([sQuery(id+"F4.wireOp",EDGE,"E43")])],"isStart":false});
            var sketch = newSketch(context, id + "F6", { "sketchPlane" : qUnion([Q0])});
            skCircle(sketch, "E44", {"center": v(0, 0) * mm, "radius": 4 * mm});
            skSolve(sketch);
        }
        {
            var Q0;
            Q0=qSketchRegion(id+"F6",true);
            extrude(context, id + "F7", {"entities" : qUnion([Q0]), "operationType" : NewBodyOperationType.REMOVE, "endBound" : BoundingType.THROUGH_ALL, "oppositeDirection" : true, "depth" : 25 * mm});
        }
        {
            var Q0;
            Q0=qCreatedBy(makeId("Right.planeOp"),FACE);
            var sketch = newSketch(context, id + "F8", { "sketchPlane" : qUnion([Q0])});
            skCircle(sketch, "E45", {"center": v(0, 11.5) * mm, "radius": 1.5 * mm});
            skSolve(sketch);
        }
        {
            var Q0;
            Q0=qSketchRegion(id+"F8",true);
            extrude(context, id + "F9", {"entities" : qUnion([Q0]), "operationType" : NewBodyOperationType.REMOVE, "endBound" : BoundingType.THROUGH_ALL, "oppositeDirection" : true, "depth" : 25 * mm});
        }
        {
            var Q0;
            Q0=makeQuery(id+"F3.opExtrude","CAP_FACE",FACE,{"disambiguationData":[OSD([sQuery(id+"F2.wireOp",EDGE,"E42")])],"isStart":false});
            var sketch = newSketch(context, id + "F10", { "sketchPlane" : qUnion([Q0])});
            skLineSegment(sketch, "E46.bottom", {"start": v(-4.47, -2.8) * mm, "end": v(-6.97, -2.8) * mm});
            skLineSegment(sketch, "E46.top", {"start": v(-4.47, 2.8) * mm, "end": v(-6.97, 2.8) * mm});
            skLineSegment(sketch, "E46.left", {"start": v(-4.47, -2.8) * mm, "end": v(-4.47, 2.8) * mm});
            skLineSegment(sketch, "E46.right", {"start": v(-6.97, -2.8) * mm, "end": v(-6.97, 2.8) * mm});
            skSolve(sketch);
        }
        {
            var Q0;
            Q0 = qSketchRegion(id + "F10", true);
            extrude(context, id + "F11", {"entities" : qUnion([Q0]), "operationType" : NewBodyOperationType.REMOVE, "oppositeDirection" : true, "depth" : 7 * mm});
        }
    });
